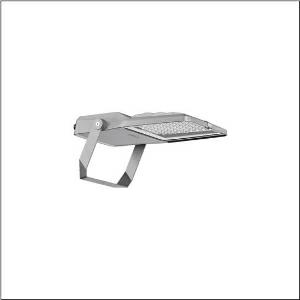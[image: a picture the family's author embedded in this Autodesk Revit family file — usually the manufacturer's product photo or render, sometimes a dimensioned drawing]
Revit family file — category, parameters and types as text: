
# Revit family: floodlight_fl_21_mini___pl43_5xa7774c2a1a_b50a
name_source: partatom
category: Lighting Fixtures
units: mm (PartAtom-declared; Revit-internal decimal feet)

## family parameters
Cut with Voids When Loaded = No
Host = Face
Light Source = No
Part Type = Normal
Room Calculation Point = No
Round Connector Dimension = Use Diameter
Shared = No

## types (1)
- --- (1 x LED, 12480 lm, 88.8 W, 3000K)
    Apparent Load = 89 VA
    CIE Flux Codes = 27 78 99 100 100
    Color Rendering = 70
    Color Temperature = 3000K
    Default Elevation = 1800 mm
    Description = Floodlight FL 21 mini, floodlight, primary light control with lens, of PMMA, primary optical cover: protective disc, of toughened safety glass, transparent, light distribution: PL43, light emission: direct distribution, installation type: surface-mounted, LED, High Power LED, rated luminous flux: 12.480lm, luminous efficacy: 141lm/W, light colour: 730, colour temperature: 3000K, control gear: DALI 2, control: overheat protection, power reduction, constant luminous flux control, flexible luminous flux parameterisation, with terminal, 6-pole, mains connection: 220..240V, AC/DC, 0/50..60Hz, start of lifetime: 89W, end of service life: 94W, reduction: 42W, luminaire housing, of diecast aluminium, powder-coated, Siteco® metallic grey (DB 702S), corrosivity category C5 mid according to DIN EN ISO 12944, chlorine-resistant, suitable for swimming pools, sealing non-destructively replaceable, mounting bracket, of steel, galvanised, powder-coated, Siteco® metallic grey (DB 702S), protection rating (complete): IP66, insulation class (complete): insulation class II (safety insulation), certification: CE, ENEC, VDE, impact resistance: IK08, permissible operating ambient temperature: -40..+40°C, permissible operating ambient temperature for outdoor applications: -40..+50°C, standard: DIN EN 12944, LABS conformity tested according to VDMA 24364:2018-05, packaging unit: 1 piece

Light Distribution: PL43
    Height = 70 mm
    Lamp = 1 x LED
    Lamp Light Flux = 12480 lm
    Lamp Power = 88.8 W
    Lamp count = 1
    Length = 485 mm
    Luminous efficacy = 141 lm/W
    Manufacturer = Siteco
    ModVariant = No
    Model = 5XA7774C2A1A
    Number of Poles = 1
    OnlyDefault = Yes
    Power Factor = 1
    Product Name = Floodlight FL 21 mini | PL43
    Product group = floodlight | pylon annexe
    ProductGroupID = 6200
    Protection Class = Protection class II
    Protection Degree = IP 66
    RLX_Detail_Level = 1
    RLX_Emergency_Light_Flux = 0 lm
    RLX_Emergency_Type = 0
    RLX_Emergency_Type_DB = No
    RlxData = <blob elided: 95989 chars, md5=07cb006c>
    Socket = socket
    Standby Power = 0 W
    System Light Flux = 12480 lm
    System Power = 89 W
    Type Comments = factory setting: luminous flux: 100 % | dim-lin: 254 | 456 mA
    Type Image = l_1006845.jpg
    URL = http://relux.com
    VarID = @adj_162234
    Voltage = 0 V
    Weight = 0.00 kg
    Width = 337 mm

## geometry (parser evidence)
native form markers: Blend x4, Sweep x14
no freeform markers — native parametric forms only
